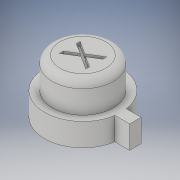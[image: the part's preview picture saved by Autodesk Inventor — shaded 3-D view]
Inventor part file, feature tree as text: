
AUTODESK INVENTOR PART (.ipt)
format: ipt  version: 2019 (Build 230136000, 136)  size: 156,160 bytes
history: native  units: mm
features: extrude x2, sketch x2, revolve x1
ambient origin geometry x8: Origin, YZ Plane, XZ Plane, XY Plane, X Axis, Y Axis, Z Axis, Center Point
bodies: Volumenkörper1 (feature_tree)
feature tree (5):
  revolve  "Umdrehung1"
  extrude  "Extrusion1"  Depth=4.0mm
  extrude  "Extrusion3"  Depth=5.0mm
  sketch  "Skizze2"  dims[d0=2.0mm d1=4.0mm]
  sketch  "Skizze4"  dims[d2=3.0mm d3=5.0mm d4=3.0mm d5=1.0mm d6=1.0mm d7=90.0deg d8=0.5mm d9=0.0mm d15=1.5mm d16=2.0mm d17=0.75mm d18=3.0mm d19=0.0mm]
